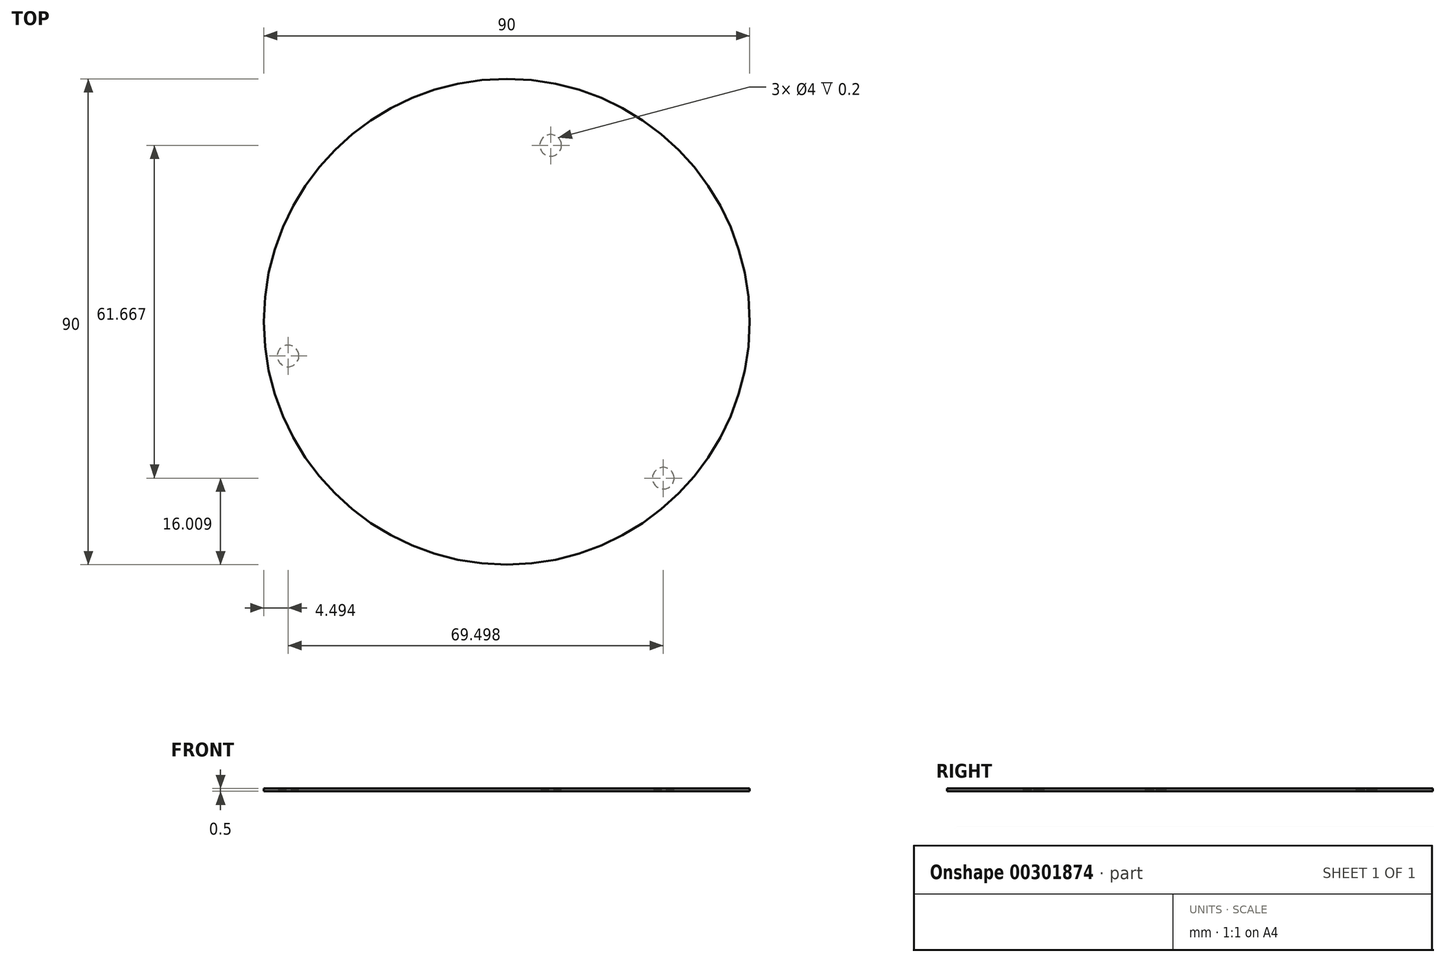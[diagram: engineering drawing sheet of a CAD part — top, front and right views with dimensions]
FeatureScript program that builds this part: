
annotation { "Feature Type Name" : "Feature", "Feature Type Description" : "" }
export const myFeature = defineFeature(function(context is Context, id is Id, definition is map)
    precondition{}
    {
        {
            var Q0;
            Q0=qCreatedBy(makeId("Top.planeOp"),FACE);
            var sketch = newSketch(context, id + "F0", { "sketchPlane" : qUnion([Q0])});
            skCircle(sketch, "E0", {"center": v(0, 0) * mm, "radius": 45 * mm});
            skCircle(sketch, "E1", {"center": v(8.13, 32.68) * mm, "radius": 2 * mm});
            skCircle(sketch, "E2", {"center": v(-40.5, -6.35) * mm, "radius": 2 * mm});
            skCircle(sketch, "E3", {"center": v(29, -29) * mm, "radius": 2 * mm});
            skSolve(sketch);
        }
        {
            var Q0;
            Q0 = qSketchRegion(id + "F0", true);
            var Q1;
            Q1=makeQuery(id+"F0.imprint","IMPRINT",FACE,{"disambiguationData":[TD([[makeQuery(id+"F0.imprint","IMPRINT",EDGE,{"derivedFrom":sQuery(id+"F0.wireOp",EDGE,"E1")}),1.0]])]});
            var Q2;
            Q2=makeQuery(id+"F0.imprint","IMPRINT",FACE,{"disambiguationData":[TD([[makeQuery(id+"F0.imprint","IMPRINT",EDGE,{"derivedFrom":sQuery(id+"F0.wireOp",EDGE,"E2")}),1.0]])]});
            var Q3;
            Q3=makeQuery(id+"F0.imprint","IMPRINT",FACE,{"disambiguationData":[TD([[makeQuery(id+"F0.imprint","IMPRINT",EDGE,{"derivedFrom":sQuery(id+"F0.wireOp",EDGE,"E3")}),1.0]])]});
            extrude(context, id + "F1", {"entities" : qUnion([Q0, Q1, Q2, Q3]), "depth" : 0.5 * mm});
        }
        {
            var Q0;
            Q0=makeQuery(id+"F0.imprint","IMPRINT",FACE,{"disambiguationData":[TD([[makeQuery(id+"F0.imprint","IMPRINT",EDGE,{"derivedFrom":sQuery(id+"F0.wireOp",EDGE,"E2")}),1.0]])]});
            var Q1;
            Q1=makeQuery(id+"F0.imprint","IMPRINT",FACE,{"disambiguationData":[TD([[makeQuery(id+"F0.imprint","IMPRINT",EDGE,{"derivedFrom":sQuery(id+"F0.wireOp",EDGE,"E1")}),1.0]])]});
            var Q2;
            Q2=makeQuery(id+"F0.imprint","IMPRINT",FACE,{"disambiguationData":[TD([[makeQuery(id+"F0.imprint","IMPRINT",EDGE,{"derivedFrom":sQuery(id+"F0.wireOp",EDGE,"E3")}),1.0]])]});
            extrude(context, id + "F2", {"entities" : qUnion([Q0, Q1, Q2]), "operationType" : NewBodyOperationType.REMOVE, "depth" : 0.2 * mm});
        }
    });
